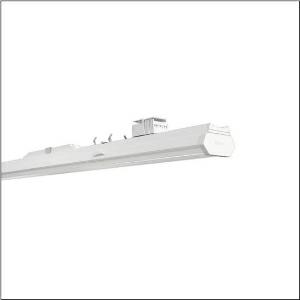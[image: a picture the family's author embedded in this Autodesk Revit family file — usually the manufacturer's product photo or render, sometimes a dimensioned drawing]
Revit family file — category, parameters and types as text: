
# Revit family: licross_r__11_protected_ho_51td12mn4f5m_c228
name_source: partatom
category: Lighting Fixtures
units: mm (PartAtom-declared; Revit-internal decimal feet)

## family parameters
Cut with Voids When Loaded = No
Host = Face
Light Source = No
Part Type = Normal
Room Calculation Point = No
Round Connector Dimension = Use Diameter
Shared = No

## types (1)
- --- (1 x LED, 15820 lm, 87.4 W, 4000K)
    Apparent Load = 87 VA
    CIE Flux Codes = 70 91 97 98 100
    Color Rendering = 80
    Color Temperature = 4000K
    Default Elevation = 1800 mm
    Description = Licross® 11 Protected HO, luminaire insert, of sheet steel, galvanised, coil coated, white, length: 1.500mm, width: 90mm, height: 101mm, LED rated luminous flux: 15.820lm, light colour: 840, control gear: ON/OFF Multilumen, with plug, 3-pole, with phase selection, mains connection: 220..240V, AC, 50/60Hz, rated input power: 87W, halogen-free wiring, primary light control with lens, of plastic, primary optical cover: cover, of PMMA, light emission: direct distribution, primary light characteristic: symmetric, protection rating (complete): IP54, insulation class (complete): insulation class I (protective earthing), certification: CE, ENEC, VDE, UKCA, protection symbol: D if used in an environment with non-conductive dust loads with corresponding accessories, impact resistance: IK06, permissible ambient temperature for indoor applications: -35..+35°C, corresponds to IFS (International Featured Standards) requirements for safety and quality in the food industry, reducing of maximum allowable ambient temperature of 5°C with ceiling mounting, LABS conformity tested according to VDMA 24364:2018-05, packaging unit: 1 piece
    Height = 92 mm
    Lamp = 1 x LED
    Lamp Light Flux = 15820 lm
    Lamp Power = 87.4 W
    Lamp count = 1
    Length = 1500 mm
    Luminous efficacy = 181 lm/W
    Manufacturer = Siteco
    ModVariant = No
    Model = 51TD12MN4F5M
    Mounting Place = Ceiling
    Mounting Type = Pendant
    Number of Poles = 1
    OnlyDefault = Yes
    Power Factor = 1
    Product Name = Licross® 11 Protected HO
    Product group = luminaire insert
    ProductGroupID = 902
    Protection Class = Protection class I
    Protection Degree = IP 54
    RLX_Detail_Level = 1
    RLX_Emergency_Light_Flux = 0 lm
    RLX_Emergency_Type = 0
    RLX_Emergency_Type_DB = No
    RlxData = <blob elided: 22149 chars, md5=803d14cc>
    Socket = socket
    Standby Power = 0 W
    System Light Flux = 15820 lm
    System Power = 87 W
    Type Comments = factory setting: luminous flux: 100 % | (A | C | E) | 203 mA
    Type Image = l_1256145.jpg
    URL = http://relux.com
    VarID = @adj_085988
    Voltage = 0 V
    Weight = 0.00 kg
    Width = 88 mm

## geometry (parser evidence)
native form markers: Blend x4, Sweep x10
no freeform markers — native parametric forms only
